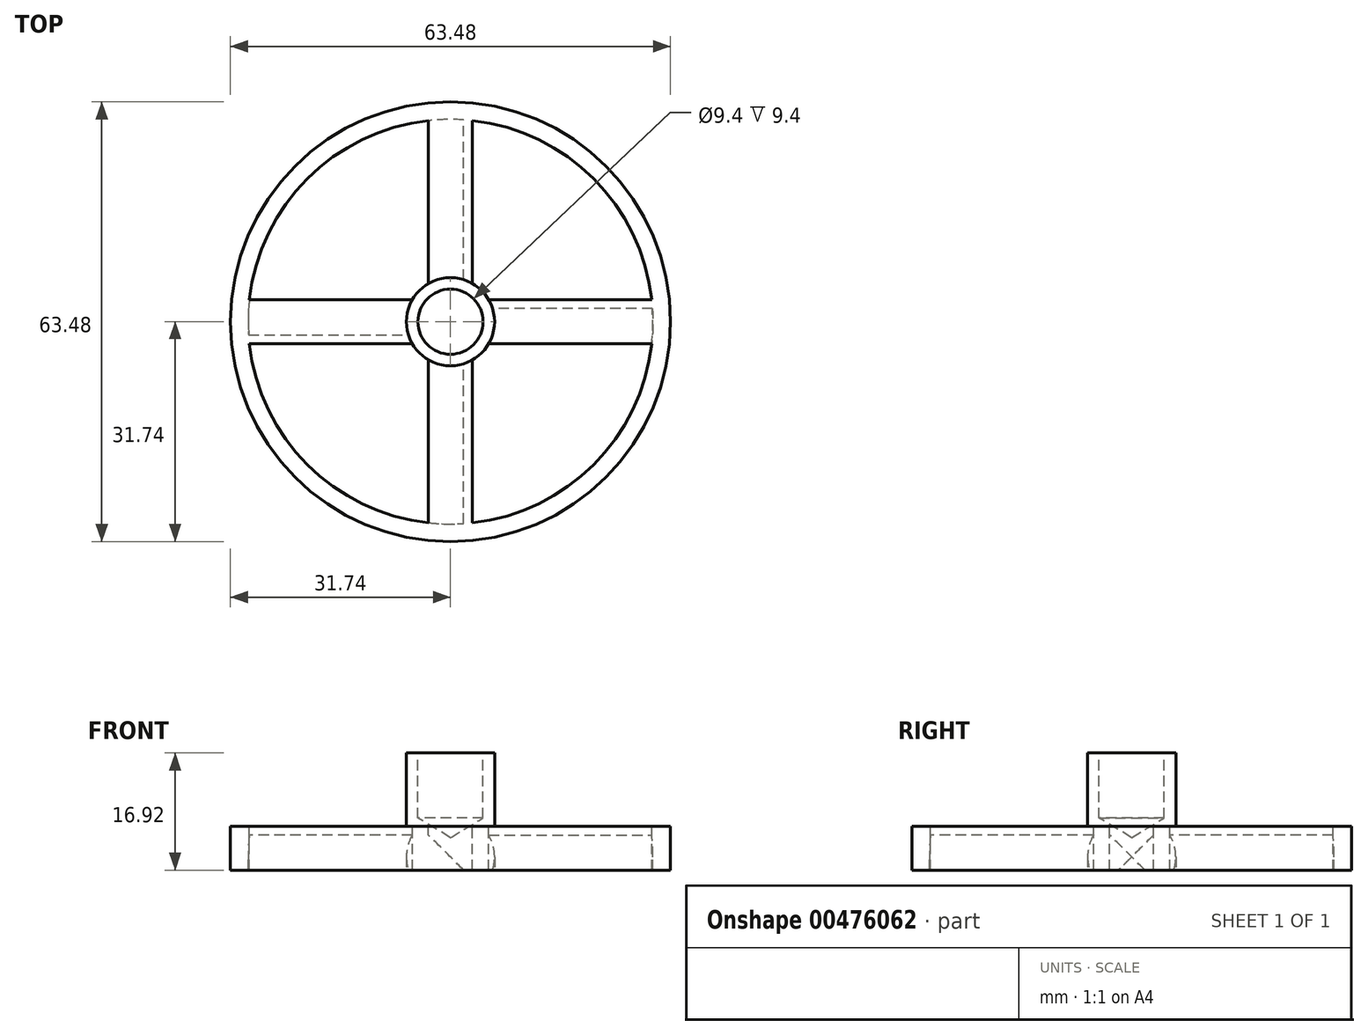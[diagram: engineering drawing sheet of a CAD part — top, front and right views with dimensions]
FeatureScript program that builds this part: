
annotation { "Feature Type Name" : "Feature", "Feature Type Description" : "" }
export const myFeature = defineFeature(function(context is Context, id is Id, definition is map)
    precondition{}
    {
        {
            var Q0;
            Q0=qCreatedBy(makeId("Front.planeOp"),FACE);
            var sketch = newSketch(context, id + "F0", { "sketchPlane" : qUnion([Q0])});
            skLineSegment(sketch, "E0", {"start": v(31.74, 6.48) * mm, "end": v(31.74, 0.13) * mm});
            skLineSegment(sketch, "E1", {"start": v(31.74, 0.13) * mm, "end": v(0, 0.13) * mm});
            skLineSegment(sketch, "E2", {"start": v(0, 0.13) * mm, "end": v(0, 17.05) * mm});
            skLineSegment(sketch, "E3.top", {"start": v(4.53, 17.05) * mm, "end": v(0, 17.05) * mm});
            skLineSegment(sketch, "E4", {"start": v(0, 17.05) * mm, "end": v(5.07, 17.05) * mm});
            skLineSegment(sketch, "E5", {"start": v(8.25, 6.48) * mm, "end": v(31.74, 6.48) * mm});
            skLineSegment(sketch, "E6", {"start": v(0, 17.05) * mm, "end": v(6.36, 17.05) * mm});
            skLineSegment(sketch, "E7", {"start": v(6.36, 17.05) * mm, "end": v(6.36, 6.48) * mm});
            skLineSegment(sketch, "E8", {"start": v(6.36, 6.48) * mm, "end": v(31.74, 6.48) * mm});
            skSolve(sketch);
        }
        {
            var Q0;
            Q0=makeQuery(id+"F0.imprint","IMPRINT",FACE,{"disambiguationData":[TD([[makeQuery(id+"F0.imprint","IMPRINT",EDGE,{"derivedFrom":sQuery(id+"F0.wireOp",EDGE,"E0")}),-1.0]])]});
            var Q1;
            Q1=sQuery(id+"F0.wireOp",EDGE,"E2");
            revolve(context, id + "F1", {"entities" : qUnion([Q0]), "axis" : qUnion([Q1]), "revolveType" : RevolveType.FULL});
        }
        {
            var Q0;
            Q0=makeQuery(id+"F1.opRevolve","SWEPT_FACE",FACE,{"disambiguationData":[OSD([sQuery(id+"F0.wireOp",EDGE,"E8")])]});
            var sketch = newSketch(context, id + "F2", { "sketchPlane" : qUnion([Q0])});
            skCircle(sketch, "E9", {"center": v(0, 0) * mm, "radius": 31.74 * mm});
            skLineSegment(sketch, "E10.bottom", {"start": v(-31.59, -3.17) * mm, "end": v(31.59, -3.17) * mm});
            skLineSegment(sketch, "E10.top", {"start": v(-31.59, 3.17) * mm, "end": v(31.59, 3.17) * mm});
            skLineSegment(sketch, "E11.left", {"start": v(3.18, -31.58) * mm, "end": v(3.18, 31.58) * mm});
            skLineSegment(sketch, "E11.right", {"start": v(-3.18, -31.58) * mm, "end": v(-3.18, 31.58) * mm});
            skArc(sketch, "E12", {"start": v(-31.59, 3.17) * mm, "mid": v(-31.74, 0) * mm, "end": v(-31.59, -3.17) * mm});
            skArc(sketch, "E13", {"start": v(-5.5, 3.17) * mm, "mid": v(-6.36, 0) * mm, "end": v(-5.5, -3.17) * mm});
            skArc(sketch, "E14", {"start": v(-3.18, -5.5) * mm, "mid": v(0, -6.36) * mm, "end": v(3.18, -5.5) * mm});
            skArc(sketch, "E15", {"start": v(5.5, 3.17) * mm, "mid": v(6.36, 0) * mm, "end": v(5.5, -3.17) * mm});
            skArc(sketch, "E16", {"start": v(3.18, 5.5) * mm, "mid": v(0, 6.36) * mm, "end": v(-3.18, 5.5) * mm});
            skCircle(sketch, "E17", {"center": v(0, 0) * mm, "radius": 29.2 * mm});
            skSolve(sketch);
        }
        {
            var Q0;
            {var subQ0=sQuery(id+"F2.wireOp",EDGE,"E10.top");var subQ3=sQuery(id+"F2.wireOp",EDGE,"E17");var subQ4=makeQuery(id+"F2.imprint","INTERSECT",VERTEX,{"disambiguationData":[OD(0.0)],"derivedFrom":[subQ0,subQ3]});Q0=makeQuery(id+"F2.imprint","IMPRINT",FACE,{"disambiguationData":[TD([[makeQuery(id+"F2.imprint","IMPRINT",EDGE,{"disambiguationData":[TD([[subQ4,1.0]])],"derivedFrom":subQ3}),1.0]])]});}
            var Q1;
            {var subQ0=sQuery(id+"F2.wireOp",EDGE,"E10.top");var subQ3=sQuery(id+"F2.wireOp",EDGE,"E17");var subQ4=makeQuery(id+"F2.imprint","INTERSECT",VERTEX,{"disambiguationData":[OD(1.0)],"derivedFrom":[subQ0,subQ3]});Q1=makeQuery(id+"F2.imprint","IMPRINT",FACE,{"disambiguationData":[TD([[makeQuery(id+"F2.imprint","IMPRINT",EDGE,{"disambiguationData":[TD([[subQ4,-1.0]])],"derivedFrom":subQ3}),1.0]])]});}
            var Q2;
            {var subQ0=sQuery(id+"F2.wireOp",EDGE,"E10.bottom");var subQ3=sQuery(id+"F2.wireOp",EDGE,"E17");var subQ4=makeQuery(id+"F2.imprint","INTERSECT",VERTEX,{"disambiguationData":[OD(1.0)],"derivedFrom":[subQ0,subQ3]});Q2=makeQuery(id+"F2.imprint","IMPRINT",FACE,{"disambiguationData":[TD([[makeQuery(id+"F2.imprint","IMPRINT",EDGE,{"disambiguationData":[TD([[subQ4,1.0]])],"derivedFrom":subQ3}),1.0]])]});}
            var Q3;
            {var subQ0=sQuery(id+"F2.wireOp",EDGE,"E10.bottom");var subQ3=sQuery(id+"F2.wireOp",EDGE,"E17");var subQ4=makeQuery(id+"F2.imprint","INTERSECT",VERTEX,{"disambiguationData":[OD(0.0)],"derivedFrom":[subQ0,subQ3]});Q3=makeQuery(id+"F2.imprint","IMPRINT",FACE,{"disambiguationData":[TD([[makeQuery(id+"F2.imprint","IMPRINT",EDGE,{"disambiguationData":[TD([[subQ4,-1.0]])],"derivedFrom":subQ3}),1.0]])]});}
            extrude(context, id + "F3", {"entities" : qUnion([Q0, Q1, Q2, Q3]), "operationType" : NewBodyOperationType.REMOVE, "oppositeDirection" : true, "depth" : 25.4 * mm});
        }
        {
            var Q0;
            {var subQ0=sQuery(id+"F2.wireOp",EDGE,"E10.bottom");Q0=makeQuery(id+"F3.boolean.opBoolean","COPY",EDGE,{"derivedFrom":makeQuery(id+"F3.opExtrude","CAP_EDGE",EDGE,{"disambiguationData":[OSD([subQ0]),TDD([makeQuery(id+"F2.imprint","IMPRINT",EDGE,{"disambiguationData":[TD([[makeQuery(id+"F2.imprint","INTERSECT",VERTEX,{"disambiguationData":[OD(0.0)],"derivedFrom":[subQ0,sQuery(id+"F2.wireOp",EDGE,"E17")]}),-1.0]])],"derivedFrom":subQ0})])],"isStart":true})});}
            var Q1;
            {var subQ0=sQuery(id+"F2.wireOp",EDGE,"E11.left");Q1=makeQuery(id+"F3.boolean.opBoolean","COPY",EDGE,{"derivedFrom":makeQuery(id+"F3.opExtrude","CAP_EDGE",EDGE,{"disambiguationData":[OSD([subQ0]),TDD([makeQuery(id+"F2.imprint","IMPRINT",EDGE,{"disambiguationData":[TD([[makeQuery(id+"F2.imprint","INTERSECT",VERTEX,{"disambiguationData":[OD(0.0)],"derivedFrom":[subQ0,sQuery(id+"F2.wireOp",EDGE,"E17")]}),-1.0]])],"derivedFrom":subQ0})])],"isStart":true})});}
            var Q2;
            {var subQ0=sQuery(id+"F2.wireOp",EDGE,"E10.top");Q2=makeQuery(id+"F3.boolean.opBoolean","COPY",EDGE,{"derivedFrom":makeQuery(id+"F3.opExtrude","CAP_EDGE",EDGE,{"disambiguationData":[OSD([subQ0]),TDD([makeQuery(id+"F2.imprint","IMPRINT",EDGE,{"disambiguationData":[TD([[makeQuery(id+"F2.imprint","INTERSECT",VERTEX,{"disambiguationData":[OD(1.0)],"derivedFrom":[subQ0,sQuery(id+"F2.wireOp",EDGE,"E17")]}),1.0]])],"derivedFrom":subQ0})])],"isStart":true})});}
            var Q3;
            {var subQ0=sQuery(id+"F2.wireOp",EDGE,"E11.left");Q3=makeQuery(id+"F3.boolean.opBoolean","COPY",EDGE,{"derivedFrom":makeQuery(id+"F3.opExtrude","CAP_EDGE",EDGE,{"disambiguationData":[OSD([subQ0]),TDD([makeQuery(id+"F2.imprint","IMPRINT",EDGE,{"disambiguationData":[TD([[makeQuery(id+"F2.imprint","INTERSECT",VERTEX,{"disambiguationData":[OD(1.0)],"derivedFrom":[subQ0,sQuery(id+"F2.wireOp",EDGE,"E17")]}),1.0]])],"derivedFrom":subQ0})])],"isStart":true})});}
            var Q4;
            {var subQ0=sQuery(id+"F2.wireOp",EDGE,"E10.top");Q4=makeQuery(id+"F3.boolean.opBoolean","INTERSECT",EDGE,{"derivedFrom":[makeQuery(id+"F1.opRevolve","SWEPT_FACE",FACE,{"disambiguationData":[OSD([sQuery(id+"F0.wireOp",EDGE,"E1")])]}),makeQuery(id+"F3.opExtrude","SWEPT_FACE",FACE,{"disambiguationData":[OSD([subQ0]),TDD([makeQuery(id+"F2.imprint","IMPRINT",EDGE,{"disambiguationData":[TD([[makeQuery(id+"F2.imprint","INTERSECT",VERTEX,{"disambiguationData":[OD(0.0)],"derivedFrom":[subQ0,sQuery(id+"F2.wireOp",EDGE,"E17")]}),-1.0]])],"derivedFrom":subQ0})])]})]});}
            var Q5;
            {var subQ0=sQuery(id+"F2.wireOp",EDGE,"E11.right");Q5=makeQuery(id+"F3.boolean.opBoolean","INTERSECT",EDGE,{"derivedFrom":[makeQuery(id+"F1.opRevolve","SWEPT_FACE",FACE,{"disambiguationData":[OSD([sQuery(id+"F0.wireOp",EDGE,"E1")])]}),makeQuery(id+"F3.opExtrude","SWEPT_FACE",FACE,{"disambiguationData":[OSD([subQ0]),TDD([makeQuery(id+"F2.imprint","IMPRINT",EDGE,{"disambiguationData":[TD([[makeQuery(id+"F2.imprint","INTERSECT",VERTEX,{"disambiguationData":[OD(0.0)],"derivedFrom":[subQ0,sQuery(id+"F2.wireOp",EDGE,"E17")]}),-1.0]])],"derivedFrom":subQ0})])]})]});}
            var Q6;
            {var subQ0=sQuery(id+"F2.wireOp",EDGE,"E10.bottom");Q6=makeQuery(id+"F3.boolean.opBoolean","INTERSECT",EDGE,{"derivedFrom":[makeQuery(id+"F1.opRevolve","SWEPT_FACE",FACE,{"disambiguationData":[OSD([sQuery(id+"F0.wireOp",EDGE,"E1")])]}),makeQuery(id+"F3.opExtrude","SWEPT_FACE",FACE,{"disambiguationData":[OSD([subQ0]),TDD([makeQuery(id+"F2.imprint","IMPRINT",EDGE,{"disambiguationData":[TD([[makeQuery(id+"F2.imprint","INTERSECT",VERTEX,{"disambiguationData":[OD(1.0)],"derivedFrom":[subQ0,sQuery(id+"F2.wireOp",EDGE,"E17")]}),1.0]])],"derivedFrom":subQ0})])]})]});}
            var Q7;
            {var subQ0=sQuery(id+"F2.wireOp",EDGE,"E11.right");Q7=makeQuery(id+"F3.boolean.opBoolean","INTERSECT",EDGE,{"derivedFrom":[makeQuery(id+"F1.opRevolve","SWEPT_FACE",FACE,{"disambiguationData":[OSD([sQuery(id+"F0.wireOp",EDGE,"E1")])]}),makeQuery(id+"F3.opExtrude","SWEPT_FACE",FACE,{"disambiguationData":[OSD([subQ0]),TDD([makeQuery(id+"F2.imprint","IMPRINT",EDGE,{"disambiguationData":[TD([[makeQuery(id+"F2.imprint","INTERSECT",VERTEX,{"disambiguationData":[OD(1.0)],"derivedFrom":[subQ0,sQuery(id+"F2.wireOp",EDGE,"E17")]}),1.0]])],"derivedFrom":subQ0})])]})]});}
            chamfer(context, id + "F4", {"entities" : qUnion([Q0, Q1, Q2, Q3, Q4, Q5, Q6, Q7]), "width" : 5.08 * mm, "tangentPropagation" : true});
        }
        {
            var Q0;
            Q0=makeQuery(id+"F1.opRevolve","SWEPT_FACE",FACE,{"disambiguationData":[OSD([sQuery(id+"F0.wireOp",EDGE,"E6")])]});
            var sketch = newSketch(context, id + "F5", { "sketchPlane" : qUnion([Q0])});
            skPoint(sketch, "E18", {"position": v(0, 0) * mm});
            skSolve(sketch);
        }
        {
            var Q0;
            Q0=sQuery(id+"F5.wireOp",VERTEX,"E18");
            var Q1;
            Q1=makeQuery(id+"F1.opRevolve","SWEPT_BODY",BODY,{"disambiguationData":[OSD([sQuery(id+"F0.wireOp",EDGE,"E0"),sQuery(id+"F0.wireOp",EDGE,"E1"),sQuery(id+"F0.wireOp",EDGE,"E2"),sQuery(id+"F0.wireOp",EDGE,"E6"),sQuery(id+"F0.wireOp",EDGE,"E7"),sQuery(id+"F0.wireOp",EDGE,"E8")])]});
            hole(context, id + "F6", {"style" : HoleStyle.SIMPLE, "endStyle" : HoleEndStyle.BLIND, "holeDiameter" : 9.4 * mm, "holeDepth" : 9.4 * mm, "isTappedThrough" : true, "tappedDepth" : 12.7 * mm, "tapClearance" : 3, "locations" : qUnion([Q0]), "scope" : qUnion([Q1])});
        }
    });
